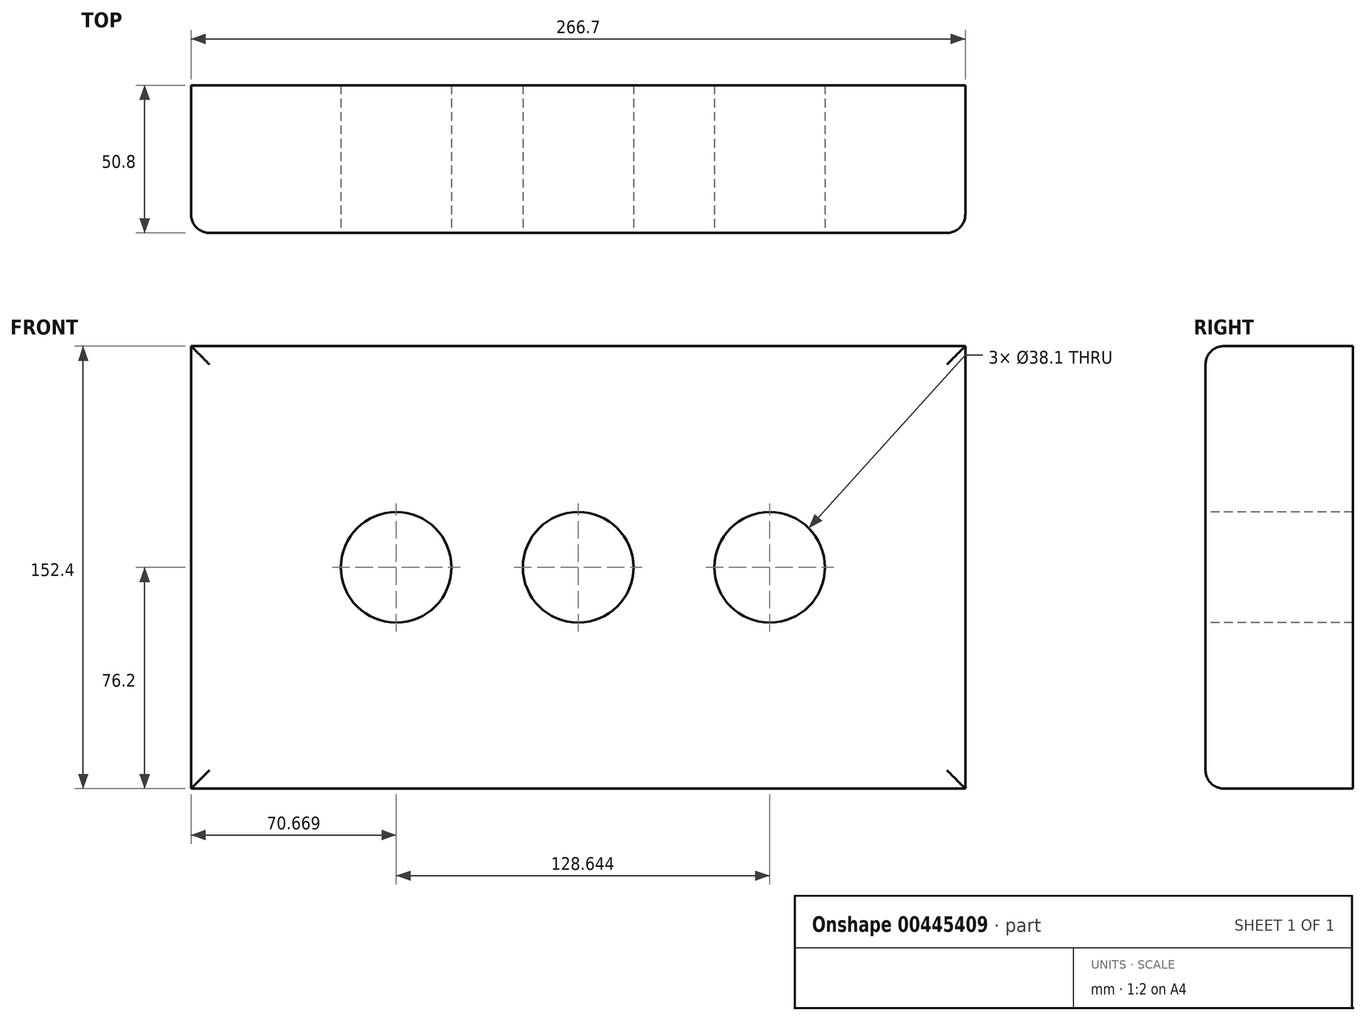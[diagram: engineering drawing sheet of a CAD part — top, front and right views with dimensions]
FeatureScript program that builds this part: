
annotation { "Feature Type Name" : "Feature", "Feature Type Description" : "" }
export const myFeature = defineFeature(function(context is Context, id is Id, definition is map)
    precondition{}
    {
        {
            var Q0;
            Q0=qCreatedBy(makeId("Front.planeOp"),FACE);
            var sketch = newSketch(context, id + "F0", { "sketchPlane" : qUnion([Q0])});
            skLineSegment(sketch, "E0.bottom", {"start": v(-133.35, 76.2) * mm, "end": v(133.35, 76.2) * mm});
            skLineSegment(sketch, "E0.top", {"start": v(-133.35, -76.2) * mm, "end": v(133.35, -76.2) * mm});
            skLineSegment(sketch, "E0.left", {"start": v(-133.35, 76.2) * mm, "end": v(-133.35, -76.2) * mm});
            skLineSegment(sketch, "E0.right", {"start": v(133.35, 76.2) * mm, "end": v(133.35, -76.2) * mm});
            skPoint(sketch, "E0.middle", {"position": v(0, 0) * mm});
            skSolve(sketch);
        }
        {
            var Q0;
            Q0=makeQuery(id+"F0.imprint","IMPRINT",FACE,{"disambiguationData":[TD([[makeQuery(id+"F0.imprint","IMPRINT",EDGE,{"derivedFrom":sQuery(id+"F0.wireOp",EDGE,"E0.bottom")}),-1.0]])]});
            extrude(context, id + "F1", {"entities" : qUnion([Q0]), "depth" : 50.8 * mm});
        }
        {
            var Q0;
            Q0=makeQuery(id+"F1.opExtrude","CAP_FACE",FACE,{"disambiguationData":[OSD([sQuery(id+"F0.wireOp",EDGE,"E0.bottom"),sQuery(id+"F0.wireOp",EDGE,"E0.top"),sQuery(id+"F0.wireOp",EDGE,"E0.left"),sQuery(id+"F0.wireOp",EDGE,"E0.right")])],"isStart":false});
            var sketch = newSketch(context, id + "F2", { "sketchPlane" : qUnion([Q0])});
            skCircle(sketch, "E1", {"center": v(0, 0) * mm, "radius": 19.05 * mm});
            skSolve(sketch);
        }
        {
            var Q0;
            Q0=makeQuery(id+"F2.imprint","IMPRINT",FACE,{"disambiguationData":[TD([[makeQuery(id+"F2.imprint","IMPRINT",EDGE,{"derivedFrom":sQuery(id+"F2.wireOp",EDGE,"E1")}),1.0]])]});
            extrude(context, id + "F3", {"entities" : qUnion([Q0]), "operationType" : NewBodyOperationType.REMOVE, "oppositeDirection" : true, "depth" : 50.8 * mm});
        }
        {
            var Q0;
            Q0=makeQuery(id+"F1.opExtrude","CAP_FACE",FACE,{"disambiguationData":[OSD([sQuery(id+"F0.wireOp",EDGE,"E0.bottom"),sQuery(id+"F0.wireOp",EDGE,"E0.top"),sQuery(id+"F0.wireOp",EDGE,"E0.left"),sQuery(id+"F0.wireOp",EDGE,"E0.right")])],"isStart":false});
            var sketch = newSketch(context, id + "F4", { "sketchPlane" : qUnion([Q0])});
            skLineSegment(sketch, "E2.bottom", {"start": v(20.24, 0) * mm, "end": v(45.64, 0) * mm});
            skLineSegment(sketch, "E2.top", {"start": v(20.24, 0) * mm, "end": v(45.64, 0) * mm});
            skLineSegment(sketch, "E2.left", {"start": v(20.24, 0) * mm, "end": v(20.24, 0) * mm});
            skLineSegment(sketch, "E2.right", {"start": v(45.64, 0) * mm, "end": v(45.64, 0) * mm});
            skLineSegment(sketch, "E3", {"start": v(-19.05, 0) * mm, "end": v(-44.45, 0) * mm});
            skSolve(sketch);
        }
        {
            var Q0;
            Q0=makeQuery(id+"F4.imprint","IMPRINT",FACE,{"disambiguationData":[TD([[makeQuery(id+"F4.imprint","IMPRINT",EDGE,{"derivedFrom":makeQuery(id+"F1.opExtrude","CAP_EDGE",EDGE,{"disambiguationData":[OSD([sQuery(id+"F0.wireOp",EDGE,"E0.bottom")])],"isStart":false})}),-1.0]])]});
            var sketch = newSketch(context, id + "F5", { "sketchPlane" : qUnion([Q0])});
            skCircle(sketch, "E4", {"center": v(65.96, 0) * mm, "radius": 19.05 * mm});
            skCircle(sketch, "E5", {"center": v(-62.68, 0) * mm, "radius": 19.05 * mm});
            skSolve(sketch);
        }
        {
            var Q0;
            Q0 = qSketchRegion(id + "F5", true);
            extrude(context, id + "F6", {"entities" : qUnion([Q0]), "operationType" : NewBodyOperationType.REMOVE, "oppositeDirection" : true, "depth" : 50.8 * mm});
        }
        {
            var Q0;
            Q0=makeQuery(id+"F1.opExtrude","CAP_EDGE",EDGE,{"disambiguationData":[OSD([sQuery(id+"F0.wireOp",EDGE,"E0.bottom")])],"isStart":false});
            var Q1;
            Q1=makeQuery(id+"F1.opExtrude","CAP_EDGE",EDGE,{"disambiguationData":[OSD([sQuery(id+"F0.wireOp",EDGE,"E0.left")])],"isStart":false});
            var Q2;
            Q2=makeQuery(id+"F1.opExtrude","CAP_EDGE",EDGE,{"disambiguationData":[OSD([sQuery(id+"F0.wireOp",EDGE,"E0.right")])],"isStart":false});
            var Q3;
            Q3=makeQuery(id+"F1.opExtrude","CAP_EDGE",EDGE,{"disambiguationData":[OSD([sQuery(id+"F0.wireOp",EDGE,"E0.top")])],"isStart":false});
            fillet(context, id + "F7", {"entities" : qUnion([Q0, Q1, Q2, Q3]), "radius" : 6.35 * mm, "tangentPropagation" : true, "allowEdgeOverflow" : false});
        }
    });
